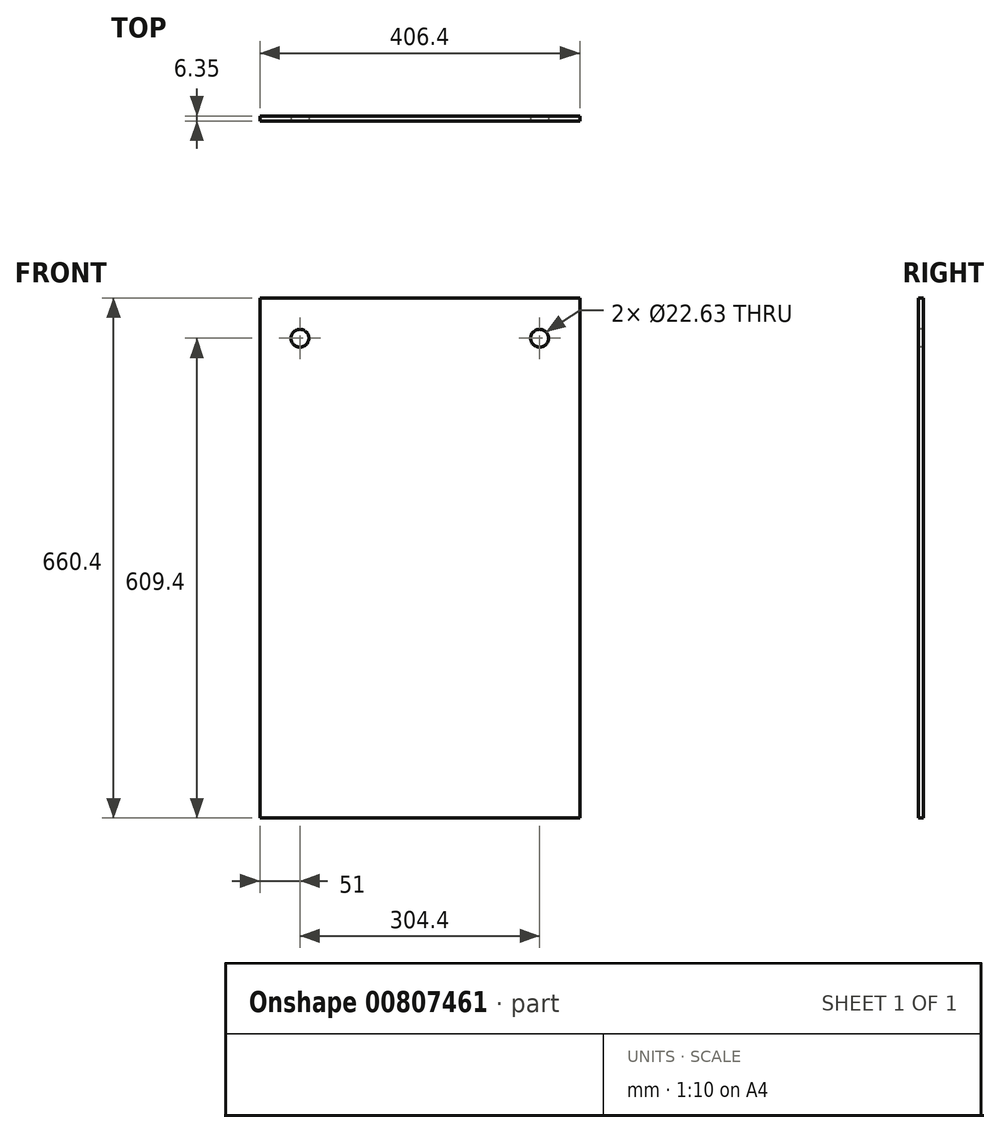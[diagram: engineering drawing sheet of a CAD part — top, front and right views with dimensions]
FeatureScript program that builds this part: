
annotation { "Feature Type Name" : "Feature", "Feature Type Description" : "" }
export const myFeature = defineFeature(function(context is Context, id is Id, definition is map)
    precondition{}
    {
        {
            var Q0;
            Q0=qCreatedBy(makeId("Front.planeOp"),FACE);
            var sketch = newSketch(context, id + "F0", { "sketchPlane" : qUnion([Q0])});
            skLineSegment(sketch, "E0.bottom", {"start": v(0, 0) * mm, "end": v(406.4, 0) * mm});
            skLineSegment(sketch, "E0.top", {"start": v(0, 660.4) * mm, "end": v(406.4, 660.4) * mm});
            skLineSegment(sketch, "E0.left", {"start": v(0, 0) * mm, "end": v(0, 660.4) * mm});
            skLineSegment(sketch, "E0.right", {"start": v(406.4, 0) * mm, "end": v(406.4, 660.4) * mm});
            skSolve(sketch);
        }
        {
            var Q0;
            Q0 = qSketchRegion(id + "F0", true);
            extrude(context, id + "F1", {"entities" : qUnion([Q0]), "depth" : 6.35 * mm, "offsetDistance" : 25.4 * mm});
        }
        {
            var Q0;
            Q0=makeQuery(id+"F1.opExtrude","CAP_FACE",FACE,{"disambiguationData":[OSD([sQuery(id+"F0.wireOp",EDGE,"E0.bottom"),sQuery(id+"F0.wireOp",EDGE,"E0.top"),sQuery(id+"F0.wireOp",EDGE,"E0.left"),sQuery(id+"F0.wireOp",EDGE,"E0.right")])],"isStart":false});
            var sketch = newSketch(context, id + "F2", { "sketchPlane" : qUnion([Q0])});
            skPoint(sketch, "E1", {"position": v(51, 609.4) * mm});
            skLineSegment(sketch, "E2", {"start": v(203.2, 660.4) * mm, "end": v(203.2, 0) * mm});
            skPoint(sketch, "E3.MirrorP", {"position": v(355.4, 609.4) * mm});
            skSolve(sketch);
        }
        {
            var Q0;
            Q0=sQuery(id+"F2.wireOp",VERTEX,"E1");
            var Q1;
            Q1=sQuery(id+"F2.wireOp",VERTEX,"E3.MirrorP");
            var Q2;
            Q2=makeQuery(id+"F1.opExtrude","SWEPT_BODY",BODY,{"disambiguationData":[OSD([sQuery(id+"F0.wireOp",EDGE,"E0.bottom"),sQuery(id+"F0.wireOp",EDGE,"E0.top"),sQuery(id+"F0.wireOp",EDGE,"E0.left"),sQuery(id+"F0.wireOp",EDGE,"E0.right")])]});
            hole(context, id + "F3", {"style" : HoleStyle.SIMPLE, "endStyle" : HoleEndStyle.THROUGH, "standardTappedOrClearance" : lookupTablePath({ "standard" : "ANSI", "fit" : "Close", "size" : "7/8", "type" : "Clearance" }), "standardBlindInLast" : lookupTablePath({ "fit" : "Close", "standard" : "ANSI", "size" : "7/8", "type" : "Clearance" }), "holeDiameter" : 22.63 * mm, "majorDiameter" : 22.22 * mm, "isTappedThrough" : true, "tappedDepth" : 12 * mm, "tapClearance" : 3, "locations" : qUnion([Q0, Q1]), "scope" : qUnion([Q2])});
        }
    });
